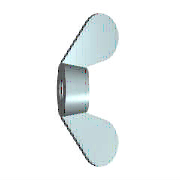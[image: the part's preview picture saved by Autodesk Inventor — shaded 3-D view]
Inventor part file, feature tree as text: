
AUTODESK INVENTOR PART (.ipt)
format: ipt  version: 2023 (Build 270158000, 158)  size: 169,472 bytes
history: native  units: mm (DEFAULTED — no unit token found)
features: sketch x2, other x2, extrude x1, mirror x1, hole x1, plane x1
ambient origin geometry x7: Origin, YZ Plane, XZ Plane, X Axis, Y Axis, Z Axis, Center Point
bodies: Solid1 (feature_tree)
feature tree (8):
  sketch  "Эскиз1"
  other  "Базовый элемент"
  extrude  "Крыло1"  Depth=12.5mm
  mirror  "Крыло2"
  hole  "Резьба"  [1 undecoded]
  other  "Work Axis1"
  plane  "Work Plane1"
  sketch  "Эскиз2"
note: 1 required parameter value undecoded (feature->parameter linkage not recoverable at this tier; creation-order binding heuristic only, values carry confidence <= 0.55)
